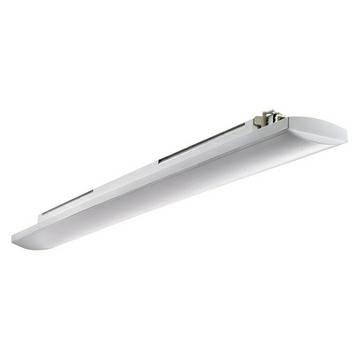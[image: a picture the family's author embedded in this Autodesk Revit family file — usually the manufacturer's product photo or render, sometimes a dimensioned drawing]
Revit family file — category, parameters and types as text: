
# Revit family: Lighting-Industrial-GEWISS-SMART[3]-WATERTIGHT-LED_OPAL_1600mm
name_source: partatom
category: Apparecchi per illuminazione
units: mm (PartAtom-declared; Revit-internal decimal feet)

## family parameters
Condiviso = No
Host = Superficie
Numero OmniClass = 23.80.70.11
Punto di calcolo locali = Sì
Quota connettore circolare = Usa diametro
Sorgente d'illuminazione = No
Taglio con vuoti quando caricato = No
Tipo di parte = Normale
Titolo OmniClass = Luminaries for Internal Lighting

## types (1)
- Lighting-Industrial-GEWISS-SMART[3]-WATERTIGHT-LED_OPAL_1600mm
    Application = Internal
    Carico apparente = 55 VA
    Catalogue = LIGHTING
    Catalogue Range = SMART [3]
    Colour temperature = 5700 K (CRI 80)
    Colour temperature: = 5700 K (CRI 80)
    Commenti sul wattaggio = 55W
    Descrizione = SMART3 1600 84LED OPALE DALI 57K LP
    Device with reduced surface temperature = Complying
    Driver type = Constant Current Driver Led
    EAN code = 8011564877207
    Efficiency class of integrated LEDs = A ÷ A++
    Electrocod = 2434
    Failure rate apparecchio (35.000h, Tq=35° C) = <2,5%
    Failure rate apparecchio (50.000h, Tq=25° C) = <2,5%
    Ganci = GEWISS  - ALLUMINIO
    Glow Wire Test = 850°C
    IDF = 23f8a58f-ab76-4331-ac73-01a839cfd15e
    IDT = e711e676-0d2c-4269-98d7-1f22e4a173c5
    IP degree = IP66/IP69
    Immagine tipo = GWS3158P.jpg
    Insulation class = II
    LED Life Time (L90B50) = 50000H
    LED Life time (L70) = 80000H
    LED Life time (L80B50) = 100000H
    LED LifeTime (L80B20) = 85000H
    Lamp = LED
    Lampada = LED
    Length = 1600 mm
    Lumen output (lm) = 6000
    Lunghezza Lampada = 1600 mm  [stored 5.24934 ft]
    Modello = GWS3258PLD57K
    No. LED (#) = 84
    Nominal flux (lm) = 6900
    Operating temperature: = -30 +50 °C
    Produttore = GEWISS S.p.A.
    Prospetto di default = 1219 mm
    SEO = Luminaire
    Schermo. = Gewiss - Led Acceso
    Shield type = Opal with feed-through wiring
    Shock resistance = IK08
    Stampa 1_100 = Sì
    Stampa 1_200 = No
    Struttura = GEWISS - SMART 3 - GRIGIO
    System power = 50W
    Technical sheet = https://www.gewiss.com
    Type of light source = LED - Not replaceable
    Typology = DALI
    URL = https://www.gewiss.com
    Version file RFA = 20.11
    Voltage = 220/240 V - 50/60 Hz - Dali
    Warranty = 5 years
    Weight (kg): = 2,5
    Working temperature = -25 +50 °C

note: [stored X ft] marks values corroborated as IEEE doubles in the binary element streams (Revit-internal decimal feet)
